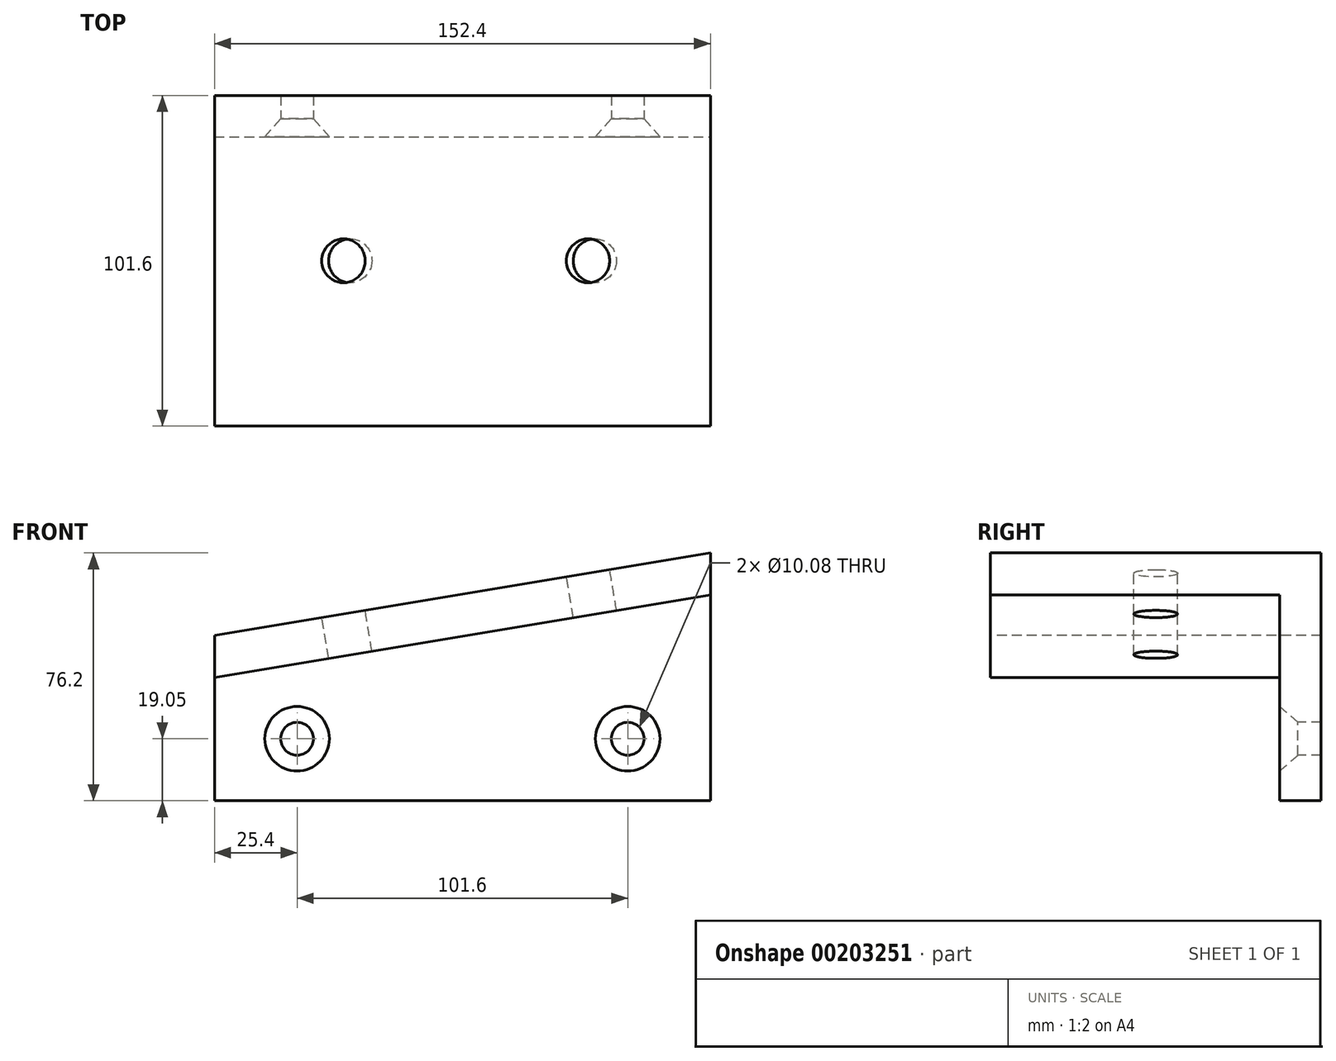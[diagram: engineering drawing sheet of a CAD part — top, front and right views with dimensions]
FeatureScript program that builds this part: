
annotation { "Feature Type Name" : "Feature", "Feature Type Description" : "" }
export const myFeature = defineFeature(function(context is Context, id is Id, definition is map)
    precondition{}
    {
        {
            var Q0;
            Q0=qCreatedBy(makeId("Front.planeOp"),FACE);
            var sketch = newSketch(context, id + "F0", { "sketchPlane" : qUnion([Q0])});
            skLineSegment(sketch, "E0.bottom", {"start": v(0, 0) * mm, "end": v(152.4, 0) * mm});
            skLineSegment(sketch, "E0.top", {"start": v(0, 101.6) * mm, "end": v(152.4, 101.6) * mm});
            skLineSegment(sketch, "E0.left", {"start": v(0, 0) * mm, "end": v(0, 101.6) * mm});
            skLineSegment(sketch, "E0.right", {"start": v(152.4, 0) * mm, "end": v(152.4, 101.6) * mm});
            skSolve(sketch);
        }
        {
            var Q0;
            Q0 = qSketchRegion(id + "F0", true);
            extrude(context, id + "F1", {"entities" : qUnion([Q0]), "depth" : 101.6 * mm});
        }
        {
            var Q0;
            Q0=makeQuery(id+"F1.opExtrude","CAP_FACE",FACE,{"disambiguationData":[OSD([sQuery(id+"F0.wireOp",EDGE,"E0.bottom"),sQuery(id+"F0.wireOp",EDGE,"E0.top"),sQuery(id+"F0.wireOp",EDGE,"E0.left"),sQuery(id+"F0.wireOp",EDGE,"E0.right")])],"isStart":false});
            var sketch = newSketch(context, id + "F2", { "sketchPlane" : qUnion([Q0])});
            skLineSegment(sketch, "E1", {"start": v(152.4, 76.2) * mm, "end": v(0, 50.8) * mm});
            skLineSegment(sketch, "E2", {"start": v(0, 50.8) * mm, "end": v(0, 101.6) * mm});
            skLineSegment(sketch, "E3", {"start": v(0, 101.6) * mm, "end": v(152.4, 101.6) * mm});
            skLineSegment(sketch, "E4", {"start": v(152.4, 101.6) * mm, "end": v(152.4, 76.2) * mm});
            skSolve(sketch);
        }
        {
            var Q0;
            Q0 = qSketchRegion(id + "F2", true);
            extrude(context, id + "F3", {"entities" : qUnion([Q0]), "operationType" : NewBodyOperationType.REMOVE, "endBound" : BoundingType.THROUGH_ALL, "oppositeDirection" : true, "depth" : 25.4 * mm});
        }
        {
            var Q0;
            Q0=makeQuery(id+"F1.opExtrude","CAP_FACE",FACE,{"disambiguationData":[OSD([sQuery(id+"F0.wireOp",EDGE,"E0.bottom"),sQuery(id+"F0.wireOp",EDGE,"E0.top"),sQuery(id+"F0.wireOp",EDGE,"E0.left"),sQuery(id+"F0.wireOp",EDGE,"E0.right")])],"isStart":false});
            var sketch = newSketch(context, id + "F4", { "sketchPlane" : qUnion([Q0])});
            skLineSegment(sketch, "E5", {"start": v(0, 0) * mm, "end": v(0, 37.92) * mm});
            skLineSegment(sketch, "E6", {"start": v(0, 37.92) * mm, "end": v(152.4, 63.32) * mm});
            skLineSegment(sketch, "E7", {"start": v(152.4, 63.32) * mm, "end": v(152.4, 0) * mm});
            skLineSegment(sketch, "E8", {"start": v(152.4, 0) * mm, "end": v(0, 0) * mm});
            skSolve(sketch);
        }
        {
            var Q0;
            Q0 = qSketchRegion(id + "F4", true);
            extrude(context, id + "F5", {"entities" : qUnion([Q0]), "operationType" : NewBodyOperationType.REMOVE, "oppositeDirection" : true, "depth" : 88.9 * mm});
        }
        {
            var Q0;
            Q0=makeQuery(id+"F5.boolean.opBoolean","COPY",FACE,{"derivedFrom":makeQuery(id+"F5.opExtrude","CAP_FACE",FACE,{"disambiguationData":[OSD([sQuery(id+"F4.wireOp",EDGE,"E5"),sQuery(id+"F4.wireOp",EDGE,"E6"),sQuery(id+"F4.wireOp",EDGE,"E7"),sQuery(id+"F4.wireOp",EDGE,"E8")])],"isStart":false})});
            var sketch = newSketch(context, id + "F6", { "sketchPlane" : qUnion([Q0])});
            skPoint(sketch, "E9", {"position": v(25.4, 19.05) * mm});
            skPoint(sketch, "E10", {"position": v(127, 19.05) * mm});
            skSolve(sketch);
        }
        {
            var Q0;
            Q0=sQuery(id+"F6.wireOp",VERTEX,"E9");
            var Q1;
            Q1=sQuery(id+"F6.wireOp",VERTEX,"E10");
            var Q2;
            Q2=makeQuery(id+"F1.opExtrude","SWEPT_BODY",BODY,{"disambiguationData":[OSD([sQuery(id+"F0.wireOp",EDGE,"E0.bottom"),sQuery(id+"F0.wireOp",EDGE,"E0.top"),sQuery(id+"F0.wireOp",EDGE,"E0.left"),sQuery(id+"F0.wireOp",EDGE,"E0.right")])]});
            hole(context, id + "F7", {"style" : HoleStyle.C_SINK, "endStyle" : HoleEndStyle.THROUGH, "standardTappedOrClearance" : lookupTablePath({ "standard" : "ANSI", "fit" : "Normal (ASME)", "size" : "3/8", "type" : "Clearance" }), "standardBlindInLast" : lookupTablePath({ "fit" : "Free", "standard" : "ANSI", "size" : "3/8", "type" : "Clearance" }), "holeDiameter" : 10.08 * mm, "cSinkDiameter" : 19.84 * mm, "cSinkAngle" : 82 * degree, "startFromSketch" : true, "locations" : qUnion([Q0, Q1]), "scope" : qUnion([Q2]), "isTappedThrough" : true});
        }
        {
            var Q0;
            Q0=makeQuery(id+"F3.boolean.opBoolean","COPY",FACE,{"derivedFrom":makeQuery(id+"F3.opExtrude","SWEPT_FACE",FACE,{"disambiguationData":[OSD([sQuery(id+"F2.wireOp",EDGE,"E1")])]})});
            var sketch = newSketch(context, id + "F8", { "sketchPlane" : qUnion([Q0])});
            skPoint(sketch, "E11", {"position": v(48.55, -50.8) * mm});
            skPoint(sketch, "E12", {"position": v(124.75, -50.8) * mm});
            skSolve(sketch);
        }
        {
            var Q0;
            Q0=sQuery(id+"F8.wireOp",VERTEX,"E12");
            var Q1;
            Q1=sQuery(id+"F8.wireOp",VERTEX,"E11");
            var Q2;
            Q2=makeQuery(id+"F1.opExtrude","SWEPT_BODY",BODY,{"disambiguationData":[OSD([sQuery(id+"F0.wireOp",EDGE,"E0.bottom"),sQuery(id+"F0.wireOp",EDGE,"E0.top"),sQuery(id+"F0.wireOp",EDGE,"E0.left"),sQuery(id+"F0.wireOp",EDGE,"E0.right")])]});
            hole(context, id + "F9", {"style" : HoleStyle.SIMPLE, "endStyle" : HoleEndStyle.THROUGH, "standardTappedOrClearance" : lookupTablePath({ "standard" : "ANSI", "fit" : "Normal (ASME)", "size" : "1/2", "type" : "Clearance" }), "standardBlindInLast" : lookupTablePath({ "fit" : "Free", "standard" : "ANSI", "size" : "1/2", "type" : "Clearance" }), "holeDiameter" : 13.5 * mm, "startFromSketch" : true, "locations" : qUnion([Q0, Q1]), "scope" : qUnion([Q2]), "isTappedThrough" : true});
        }
    });
